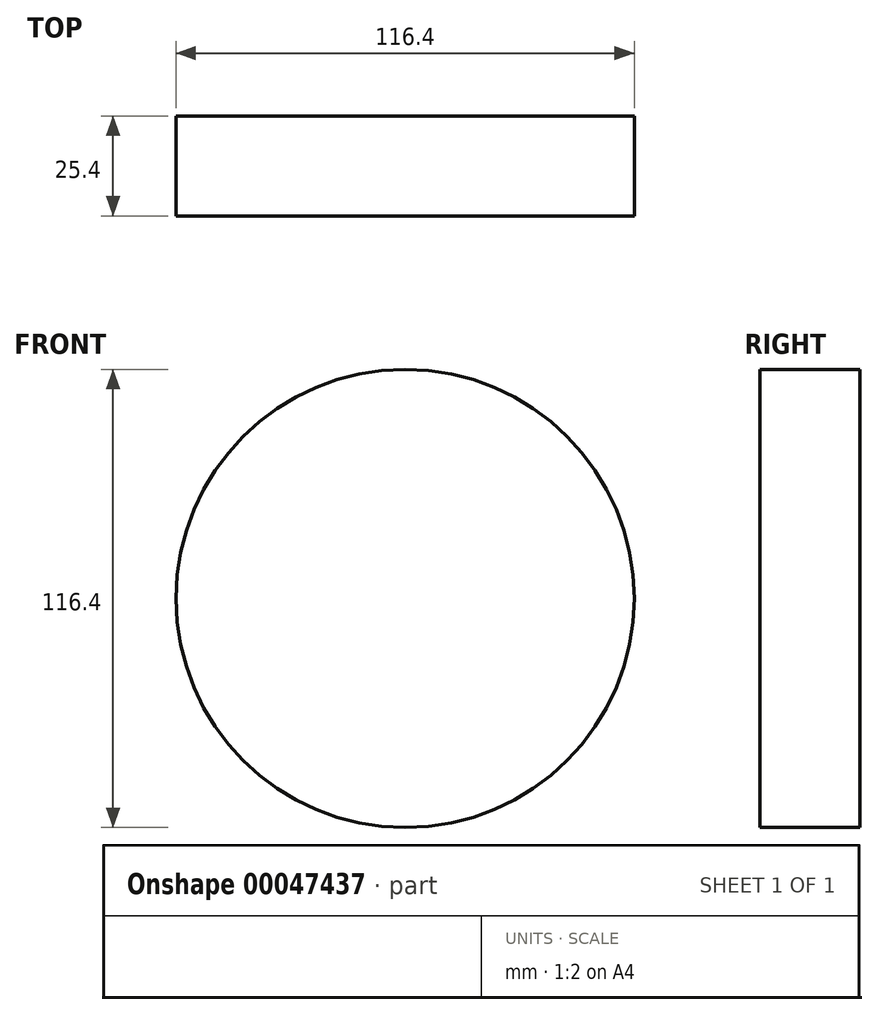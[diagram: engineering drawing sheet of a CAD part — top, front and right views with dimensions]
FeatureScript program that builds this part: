
annotation { "Feature Type Name" : "Feature", "Feature Type Description" : "" }
export const myFeature = defineFeature(function(context is Context, id is Id, definition is map)
    precondition{}
    {
        {
            var Q0;
            Q0=qCreatedBy(makeId("Front.planeOp"),FACE);
            var sketch = newSketch(context, id + "F0", { "sketchPlane" : qUnion([Q0])});
            skCircle(sketch, "E0", {"center": v(0, 0) * mm, "radius": 58.2 * mm});
            skSolve(sketch);
        }
        {
            var Q0;
            Q0=makeQuery(id+"F0.imprint","IMPRINT",FACE,{"disambiguationData":[TD([[makeQuery(id+"F0.imprint","IMPRINT",EDGE,{"derivedFrom":sQuery(id+"F0.wireOp",EDGE,"E0")}),1.0]])]});
            extrude(context, id + "F1", {"entities" : qUnion([Q0]), "endBound" : BoundingType.SYMMETRIC, "depth" : 25.4 * mm});
        }
    });
